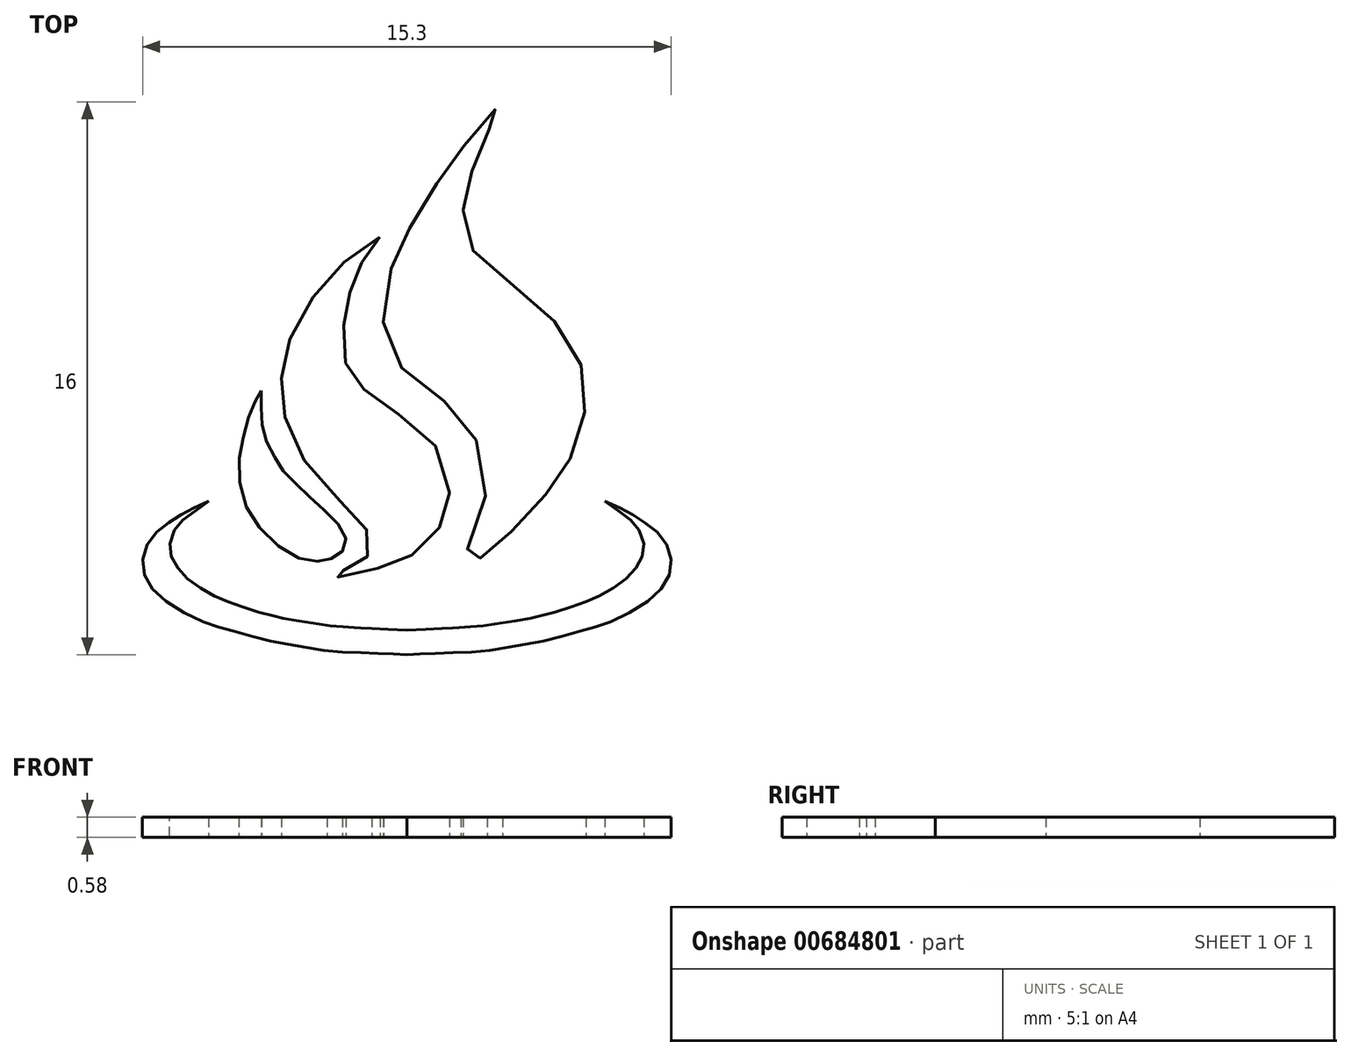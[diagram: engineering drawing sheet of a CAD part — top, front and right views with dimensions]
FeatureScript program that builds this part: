
annotation { "Feature Type Name" : "Feature", "Feature Type Description" : "" }
export const myFeature = defineFeature(function(context is Context, id is Id, definition is map)
    precondition{}
    {
        {
            var Q0;
            Q0=qCreatedBy(makeId("Top.planeOp"),FACE);
            var sketch = newSketch(context, id + "F0", { "sketchPlane" : qUnion([Q0])});
            skFitSpline(sketch, "E0", {"points": [v(-4.34, 0.82) * mm, v(-4.46, 0.63) * mm, v(-4.64, 0.22) * mm, v(-4.85, -0.47) * mm, v(-4.98, -1.25) * mm, v(-4.85, -2.33) * mm, v(-4.3, -3.24) * mm, v(-3.4, -3.96) * mm, v(-2.75, -4.12) * mm, v(-2.4, -4.07) * mm, v(-2.08, -3.92) * mm, v(-1.9, -3.66) * mm, v(-1.92, -3.35) * mm, v(-2.25, -2.88) * mm, v(-2.77, -2.41) * mm, v(-3.2, -1.99) * mm, v(-3.65, -1.55) * mm, v(-3.9, -1.18) * mm, v(-4.17, -0.7) * mm, v(-4.3, -0.2) * mm, v(-4.33, 0.35) * mm, v(-4.34, 0.82) * mm]});
            skFitSpline(sketch, "E1", {"points": [v(-0.9, 5.27) * mm, v(-1.5, 4.88) * mm, v(-2.02, 4.46) * mm, v(-2.6, 3.81) * mm, v(-3.08, 3.2) * mm, v(-3.5, 2.37) * mm, v(-3.67, 1.8) * mm, v(-3.76, 1.18) * mm, v(-3.73, 0.57) * mm, v(-3.65, 0.07) * mm, v(-3.38, -0.64) * mm, v(-2.9, -1.48) * mm, v(-2.13, -2.3) * mm, v(-1.5, -2.93) * mm, v(-1.34, -3.13) * mm, v(-1.17, -3.39) * mm, v(-1.13, -3.6) * mm, v(-1.26, -3.96) * mm, v(-1.57, -4.17) * mm, v(-1.78, -4.3) * mm, v(-1.99, -4.4) * mm, v(-2.27, -4.5) * mm, v(-2.43, -4.57) * mm, v(-1.76, -4.54) * mm, v(-1.24, -4.4) * mm, v(-0.79, -4.27) * mm, v(-0.23, -4.06) * mm, v(0.1, -3.88) * mm, v(0.54, -3.45) * mm, v(0.86, -3.05) * mm, v(1.03, -2.62) * mm, v(1.1, -2.1) * mm, v(0.97, -1.24) * mm, v(0.4, -0.41) * mm, v(-0.25, 0.08) * mm, v(-1, 0.56) * mm, v(-1.37, 0.87) * mm, v(-1.62, 1.13) * mm, v(-1.83, 1.48) * mm, v(-1.97, 1.88) * mm, v(-1.97, 2.5) * mm, v(-1.93, 2.91) * mm, v(-1.88, 3.26) * mm, v(-1.75, 3.76) * mm, v(-1.65, 4.04) * mm, v(-1.51, 4.37) * mm, v(-1.17, 4.95) * mm, v(-1, 5.15) * mm, v(-0.9, 5.27) * mm]});
            skFitSpline(sketch, "E2", {"points": [v(1.46, -4.37) * mm, v(1.7, -4.24) * mm, v(1.84, -4.14) * mm, v(2.21, -3.86) * mm, v(2.46, -3.64) * mm, v(2.77, -3.4) * mm, v(2.94, -3.22) * mm, v(3.42, -2.74) * mm, v(3.77, -2.34) * mm, v(4, -2.05) * mm, v(4.22, -1.73) * mm, v(4.48, -1.36) * mm, v(4.68, -1) * mm, v(4.9, -0.4) * mm, v(4.99, 0.01) * mm, v(5.06, 0.53) * mm, v(5.03, 1.02) * mm, v(4.94, 1.48) * mm, v(4.79, 1.88) * mm, v(4.48, 2.43) * mm, v(4.05, 2.93) * mm, v(3.55, 3.43) * mm, v(2.9, 3.91) * mm, v(2.4, 4.3) * mm, v(2.08, 4.58) * mm, v(1.75, 4.94) * mm, v(1.57, 5.37) * mm, v(1.51, 5.83) * mm, v(1.5, 6.02) * mm, v(1.54, 6.36) * mm, v(1.6, 6.68) * mm, v(1.7, 7.02) * mm, v(1.83, 7.38) * mm, v(2, 7.85) * mm, v(2.15, 8.18) * mm, v(2.36, 8.61) * mm, v(2.52, 8.94) * mm, v(2.64, 9.18) * mm, v(2.21, 8.72) * mm, v(1.9, 8.35) * mm, v(1.68, 8.08) * mm, v(1.43, 7.79) * mm, v(1.16, 7.44) * mm, v(0.85, 6.98) * mm, v(0.6, 6.62) * mm, v(0.24, 6.05) * mm, v(-0.03, 5.55) * mm, v(-0.26, 5.18) * mm, v(-0.43, 4.75) * mm, v(-0.56, 4.4) * mm, v(-0.78, 3.68) * mm, v(-0.8, 3.01) * mm, v(-0.8, 2.66) * mm, v(-0.58, 2) * mm, v(-0.36, 1.58) * mm, v(0, 1.26) * mm, v(0.6, 0.87) * mm, v(1.05, 0.43) * mm, v(1.53, -0.02) * mm, v(1.78, -0.47) * mm, v(2.02, -0.83) * mm, v(2.2, -1.6) * mm, v(2.13, -2.38) * mm, v(1.99, -3) * mm, v(1.74, -3.51) * mm, v(1.46, -4.37) * mm]});
            skFitSpline(sketch, "E3", {"points": [v(-5.86, -2.38) * mm, v(-6.5, -2.83) * mm, v(-6.85, -3.22) * mm, v(-6.99, -3.76) * mm, v(-6.82, -4.2) * mm, v(-6.43, -4.66) * mm, v(-5.8, -5.07) * mm, v(-5.22, -5.31) * mm, v(-4.46, -5.57) * mm, v(-3.89, -5.72) * mm, v(-3.54, -5.8) * mm, v(-2.51, -5.95) * mm, v(-2.28, -5.98) * mm, v(-1.72, -6.03) * mm, v(-1.59, -6.04) * mm, v(-1.44, -6.05) * mm, v(-1.07, -6.07) * mm, v(-0.12, -6.1) * mm], "startDerivative": vector(-8.08, -5.54) * mm, "endDerivative": vector(12.44, -0.4) * mm});
            skFitSpline(sketch, "E4", {"points": [v(-5.86, -2.38) * mm, v(-6.5, -2.67) * mm, v(-7, -2.98) * mm, v(-7.5, -3.42) * mm, v(-7.77, -4.07) * mm, v(-7.62, -4.72) * mm, v(-6.98, -5.35) * mm, v(-5.86, -5.93) * mm, v(-5.23, -6.1) * mm, v(-4.23, -6.4) * mm, v(-3.35, -6.54) * mm, v(-2.42, -6.7) * mm, v(-1.44, -6.76) * mm, v(-0.66, -6.8) * mm, v(-0.12, -6.82) * mm], "startDerivative": vector(-9.85, -4.17) * mm, "endDerivative": vector(8.78, -0.47) * mm});
            skFitSpline(sketch, "E5.MirrorCS", {"points": [v(5.61, -2.38) * mm, v(6.24, -2.83) * mm, v(6.6, -3.22) * mm, v(6.74, -3.76) * mm, v(6.57, -4.2) * mm, v(6.18, -4.66) * mm, v(5.55, -5.07) * mm, v(4.97, -5.31) * mm, v(4.21, -5.57) * mm, v(3.64, -5.72) * mm, v(3.3, -5.8) * mm, v(2.27, -5.95) * mm, v(2.03, -5.98) * mm, v(1.47, -6.03) * mm, v(1.34, -6.04) * mm, v(1.2, -6.05) * mm, v(0.82, -6.07) * mm, v(-0.12, -6.1) * mm], "startDerivative": vector(8.08, -5.54) * mm, "endDerivative": vector(-12.44, -0.4) * mm});
            skFitSpline(sketch, "E6.MirrorCS", {"points": [v(5.61, -2.38) * mm, v(6.24, -2.67) * mm, v(6.75, -2.98) * mm, v(7.26, -3.42) * mm, v(7.52, -4.07) * mm, v(7.37, -4.72) * mm, v(6.73, -5.35) * mm, v(5.61, -5.93) * mm, v(4.98, -6.1) * mm, v(3.98, -6.4) * mm, v(3.1, -6.54) * mm, v(2.17, -6.7) * mm, v(1.2, -6.76) * mm, v(0.41, -6.8) * mm, v(-0.12, -6.82) * mm], "startDerivative": vector(9.85, -4.17) * mm, "endDerivative": vector(-8.78, -0.47) * mm});
            skLineSegment(sketch, "E7", {"start": v(-0.05, 2.16) * mm, "end": v(-0.05, 10.67) * mm});
            skSolve(sketch);
        }
        {
            var Q0;
            Q0 = qSketchRegion(id + "F0", true);
            extrude(context, id + "F1", {"entities" : qUnion([Q0]), "depth" : 0.58 * mm, "offsetDistance" : 25.4 * mm});
        }
    });
